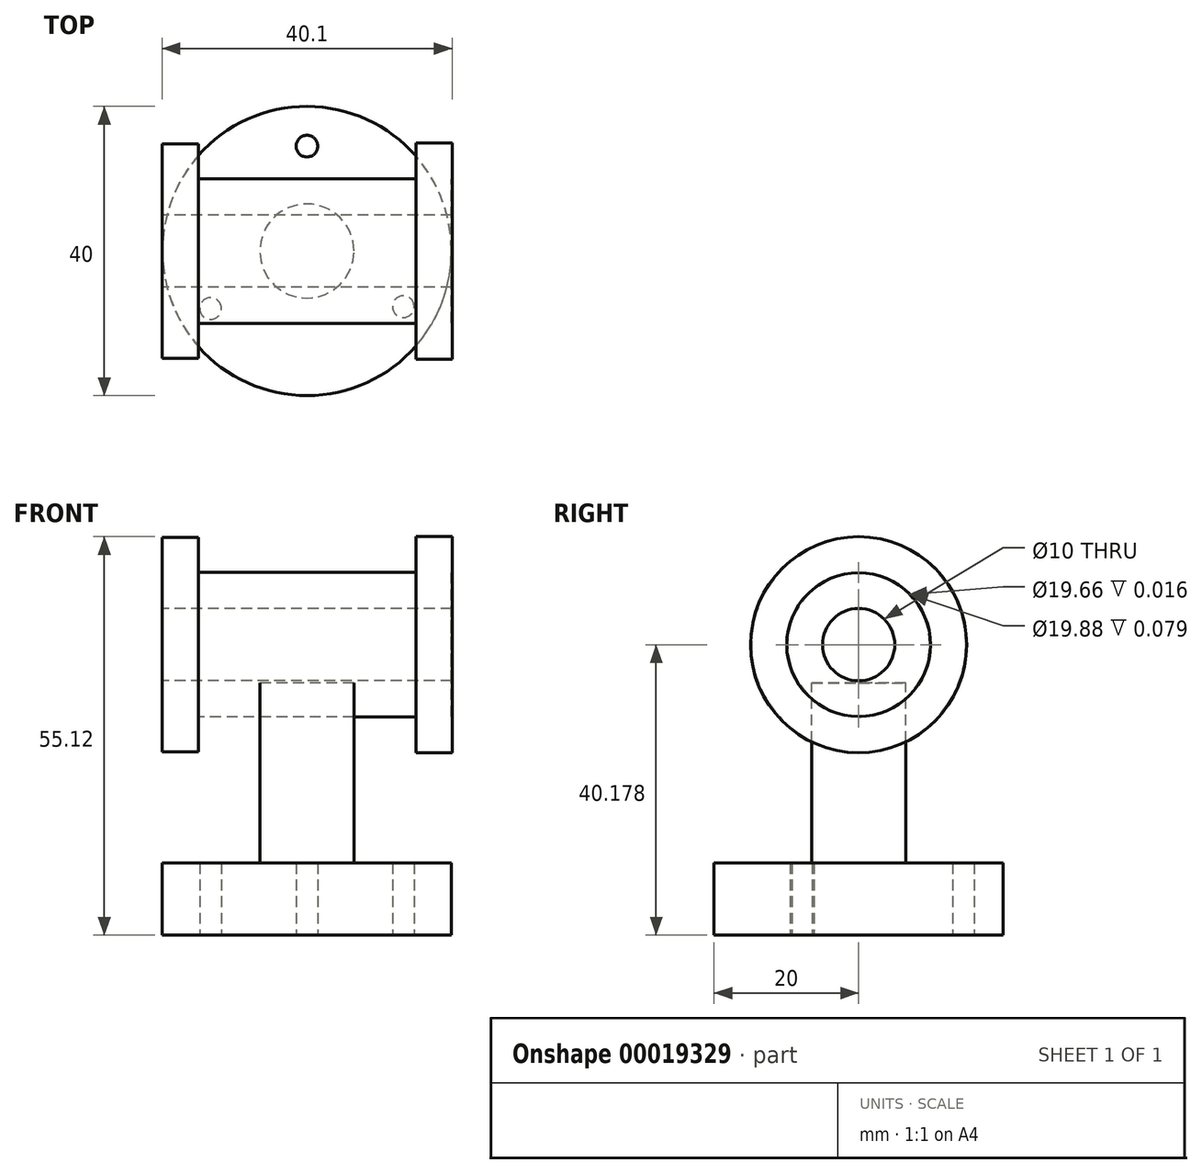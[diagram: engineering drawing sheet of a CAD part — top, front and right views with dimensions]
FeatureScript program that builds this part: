
annotation { "Feature Type Name" : "Feature", "Feature Type Description" : "" }
export const myFeature = defineFeature(function(context is Context, id is Id, definition is map)
    precondition{}
    {
        {
            var Q0;
            Q0=qCreatedBy(makeId("Top.planeOp"),FACE);
            var sketch = newSketch(context, id + "F0", { "sketchPlane" : qUnion([Q0])});
            skCircle(sketch, "E0", {"center": v(0, 0) * mm, "radius": 20 * mm});
            skCircle(sketch, "E1", {"center": v(0, 14.5) * mm, "radius": 1.5 * mm});
            skCircle(sketch, "E2", {"center": v(13.33, -7.7) * mm, "radius": 1.5 * mm});
            skCircle(sketch, "E3", {"center": v(-13.33, -7.96) * mm, "radius": 1.5 * mm});
            skCircle(sketch, "E4", {"center": v(0, 0) * mm, "radius": 6.5 * mm});
            skSolve(sketch);
        }
        {
            var Q0;
            Q0=makeQuery(id+"F0.imprint","IMPRINT",FACE,{"disambiguationData":[TD([[makeQuery(id+"F0.imprint","IMPRINT",EDGE,{"derivedFrom":sQuery(id+"F0.wireOp",EDGE,"E0")}),1.0]])]});
            var Q1;
            Q1=makeQuery(id+"F0.imprint","IMPRINT",FACE,{"disambiguationData":[TD([[makeQuery(id+"F0.imprint","IMPRINT",EDGE,{"derivedFrom":sQuery(id+"F0.wireOp",EDGE,"E4")}),1.0]])]});
            extrude(context, id + "F1", {"entities" : qUnion([Q0, Q1]), "depth" : 10 * mm});
        }
        {
            var Q0;
            Q0=makeQuery(id+"F1.opExtrude","CAP_FACE",FACE,{"disambiguationData":[OSD([sQuery(id+"F0.wireOp",EDGE,"E0"),sQuery(id+"F0.wireOp",EDGE,"E1"),sQuery(id+"F0.wireOp",EDGE,"E2"),sQuery(id+"F0.wireOp",EDGE,"E3")])],"isStart":false});
            var sketch = newSketch(context, id + "F2", { "sketchPlane" : qUnion([Q0])});
            skCircle(sketch, "E5", {"center": v(0, 0) * mm, "radius": 6.5 * mm});
            skSolve(sketch);
        }
        {
            var Q0;
            Q0=qCreatedBy(makeId("Right.planeOp"),FACE);
            var sketch = newSketch(context, id + "F3", { "sketchPlane" : qUnion([Q0])});
            skCircle(sketch, "E6", {"center": v(0, 40.18) * mm, "radius": 5 * mm});
            skCircle(sketch, "E7", {"center": v(0, 40.18) * mm, "radius": 10 * mm});
            skSolve(sketch);
        }
        {
            var Q0;
            Q0=makeQuery(id+"F3.imprint","IMPRINT",FACE,{"disambiguationData":[TD([[makeQuery(id+"F3.imprint","IMPRINT",EDGE,{"derivedFrom":sQuery(id+"F3.wireOp",EDGE,"E6")}),-1.0]])]});
            extrude(context, id + "F4", {"entities" : qUnion([Q0]), "depth" : 20 * mm, "hasSecondDirection" : true, "secondDirectionOppositeDirection" : true, "secondDirectionDepth" : 20 * mm});
        }
        {
            var Q0;
            Q0=qCreatedBy(makeId("Right.planeOp"),FACE);
            var sketch = newSketch(context, id + "F5", { "sketchPlane" : qUnion([Q0])});
            skLineSegment(sketch, "E8", {"start": v(0, 10.29) * mm, "end": v(0, 35.17) * mm});
            skSolve(sketch);
        }
        {
            var Q0;
            Q0=makeQuery(id+"F2.imprint","IMPRINT",FACE,{"disambiguationData":[TD([[makeQuery(id+"F2.imprint","IMPRINT",EDGE,{"derivedFrom":sQuery(id+"F2.wireOp",EDGE,"E5")}),1.0]])]});
            var Q1;
            Q1=sQuery(id+"F5.wireOp",EDGE,"E8");
            sweep(context, id + "F6", {"profiles" : qUnion([Q0]), "path" : qUnion([Q1])});
        }
        {
            var Q0;
            Q0=qCreatedBy(makeId("Front.planeOp"),FACE);
            var sketch = newSketch(context, id + "F7", { "sketchPlane" : qUnion([Q0])});
            skLineSegment(sketch, "E9.bottom", {"start": v(-20.02, 50) * mm, "end": v(-15.02, 50) * mm});
            skLineSegment(sketch, "E9.top", {"start": v(-20.02, 55) * mm, "end": v(-15.02, 55) * mm});
            skLineSegment(sketch, "E9.left", {"start": v(-20.02, 50) * mm, "end": v(-20.02, 55) * mm});
            skLineSegment(sketch, "E9.right", {"start": v(-15.02, 50) * mm, "end": v(-15.02, 55) * mm});
            skLineSegment(sketch, "E10.bottom", {"start": v(15.08, 50.12) * mm, "end": v(20.08, 50.12) * mm});
            skLineSegment(sketch, "E10.top", {"start": v(15.08, 55.12) * mm, "end": v(20.08, 55.12) * mm});
            skLineSegment(sketch, "E10.left", {"start": v(15.08, 50.12) * mm, "end": v(15.08, 55.12) * mm});
            skLineSegment(sketch, "E10.right", {"start": v(20.08, 50.12) * mm, "end": v(20.08, 55.12) * mm});
            skSolve(sketch);
        }
        {
            var Q0;
            Q0 = qSketchRegion(id + "F7", true);
            var Q1;
            Q1=makeQuery(id+"F4.opExtrude","SWEPT_FACE",FACE,{"disambiguationData":[OSD([sQuery(id+"F3.wireOp",EDGE,"E7")])]});
            revolve(context, id + "F8", {"operationType" : NewBodyOperationType.ADD, "entities" : qUnion([Q0]), "axis" : qUnion([Q1]), "revolveType" : RevolveType.FULL});
        }
    });
